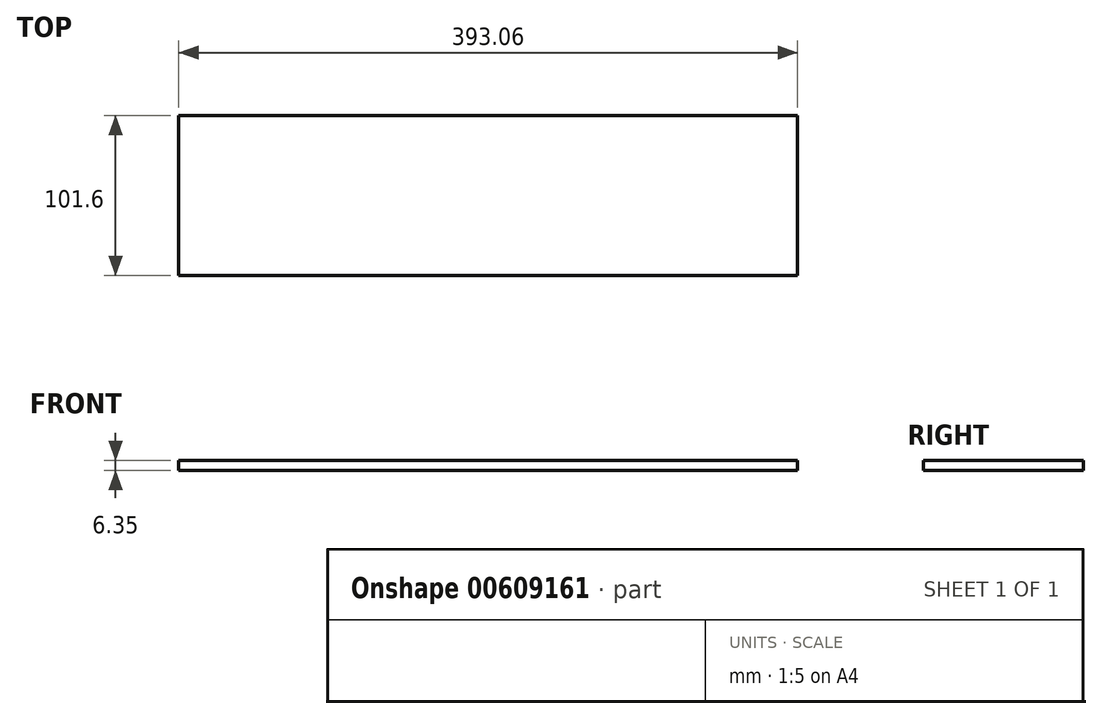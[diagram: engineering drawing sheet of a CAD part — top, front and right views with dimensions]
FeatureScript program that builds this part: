
annotation { "Feature Type Name" : "Feature", "Feature Type Description" : "" }
export const myFeature = defineFeature(function(context is Context, id is Id, definition is map)
    precondition{}
    {
        {
            var Q0;
            Q0=qCreatedBy(makeId("Top.planeOp"),FACE);
            var sketch = newSketch(context, id + "F0", { "sketchPlane" : qUnion([Q0])});
            skLineSegment(sketch, "E0.bottom", {"start": v(0, 0) * mm, "end": v(393.06, 0) * mm});
            skLineSegment(sketch, "E0.top", {"start": v(0, 101.6) * mm, "end": v(393.06, 101.6) * mm});
            skLineSegment(sketch, "E0.left", {"start": v(0, 0) * mm, "end": v(0, 101.6) * mm});
            skLineSegment(sketch, "E0.right", {"start": v(393.06, 0) * mm, "end": v(393.06, 101.6) * mm});
            skSolve(sketch);
        }
        {
            var Q0;
            Q0=makeQuery(id+"F0.imprint","IMPRINT",FACE,{"disambiguationData":[TD([[makeQuery(id+"F0.imprint","IMPRINT",EDGE,{"derivedFrom":sQuery(id+"F0.wireOp",EDGE,"E0.bottom")}),1.0]])]});
            extrude(context, id + "F1", {"entities" : qUnion([Q0]), "depth" : 6.35 * mm, "offsetDistance" : 25.4 * mm});
        }
    });
